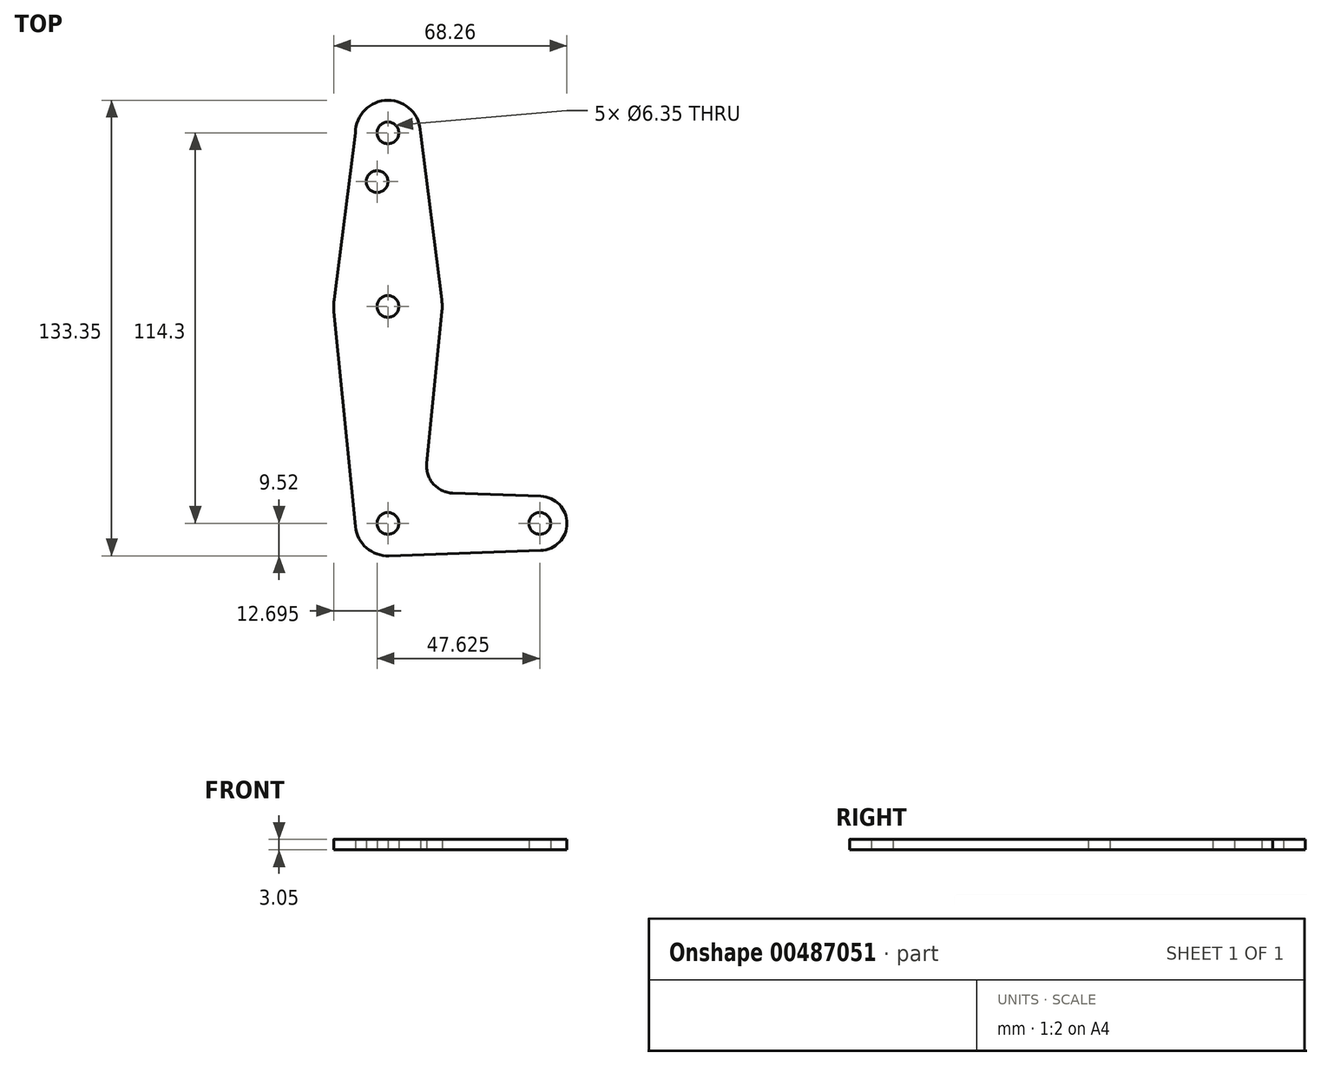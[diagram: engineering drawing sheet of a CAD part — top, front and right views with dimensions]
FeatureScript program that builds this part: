
annotation { "Feature Type Name" : "Feature", "Feature Type Description" : "" }
export const myFeature = defineFeature(function(context is Context, id is Id, definition is map)
    precondition{}
    {
        {
            var Q0;
            Q0=qCreatedBy(makeId("Top.planeOp"),FACE);
            var sketch = newSketch(context, id + "F0", { "sketchPlane" : qUnion([Q0])});
            skLineSegment(sketch, "E0", {"start": v(0, 0) * mm, "end": v(0, 114.3) * mm, "construction": true});
            skLineSegment(sketch, "E1", {"start": v(0, 0) * mm, "end": v(44.45, 0) * mm, "construction": true});
            skCircle(sketch, "E2", {"center": v(0, 0) * mm, "radius": 9.53 * mm});
            skCircle(sketch, "E3", {"center": v(0, 114.3) * mm, "radius": 9.53 * mm});
            skCircle(sketch, "E4", {"center": v(44.45, 0) * mm, "radius": 7.94 * mm});
            skCircle(sketch, "E5", {"center": v(0, 63.5) * mm, "radius": 15.88 * mm});
            skLineSegment(sketch, "E6", {"start": v(9.52, 114.3) * mm, "end": v(15.75, 65.5) * mm});
            skLineSegment(sketch, "E7", {"start": v(-9.52, 114.3) * mm, "end": v(-15.75, 65.5) * mm});
            skPoint(sketch, "E8.startSnap0", {"position": v(0, 57.15) * mm});
            skLineSegment(sketch, "E9", {"start": v(15.8, 61.91) * mm, "end": v(11.34, 17.6) * mm});
            skLineSegment(sketch, "E10", {"start": v(-15.8, 61.91) * mm, "end": v(-9.48, -0.95) * mm});
            skLineSegment(sketch, "E11", {"start": v(18.97, 8.85) * mm, "end": v(44.73, 7.93) * mm});
            skLineSegment(sketch, "E12", {"start": v(0.34, -9.52) * mm, "end": v(44.73, -7.93) * mm});
            skCircle(sketch, "E13", {"center": v(0, 114.3) * mm, "radius": 3.18 * mm});
            skCircle(sketch, "E14", {"center": v(0, 63.5) * mm, "radius": 3.18 * mm});
            skCircle(sketch, "E15", {"center": v(0, 0) * mm, "radius": 3.18 * mm});
            skCircle(sketch, "E16", {"center": v(44.45, 0) * mm, "radius": 3.18 * mm});
            skCircle(sketch, "E17", {"center": v(-3.18, 100.03) * mm, "radius": 3.18 * mm});
            skArc(sketch, "E18.filletArc", {"start": v(11.34, 17.6) * mm, "mid": v(13.26, 11.57) * mm, "end": v(18.97, 8.85) * mm});
            skSolve(sketch);
        }
        {
            var Q0;
            Q0=makeQuery(id+"F0.imprint","IMPRINT",FACE,{"disambiguationData":[TD([[makeQuery(id+"F0.imprint","IMPRINT",EDGE,{"derivedFrom":sQuery(id+"F0.wireOp",EDGE,"E13")}),-1.0]])]});
            var Q1;
            {var subQ0=sQuery(id+"F0.wireOp",EDGE,"E6");Q1=makeQuery(id+"F0.imprint","IMPRINT",FACE,{"disambiguationData":[TD([[makeQuery(id+"F0.imprint","IMPRINT",EDGE,{"derivedFrom":subQ0}),-1.0]])]});}
            var Q2;
            Q2=makeQuery(id+"F0.imprint","IMPRINT",FACE,{"disambiguationData":[TD([[makeQuery(id+"F0.imprint","IMPRINT",EDGE,{"derivedFrom":sQuery(id+"F0.wireOp",EDGE,"E14")}),-1.0]])]});
            var Q3;
            {var subQ0=sQuery(id+"F0.wireOp",EDGE,"E9");Q3=makeQuery(id+"F0.imprint","IMPRINT",FACE,{"disambiguationData":[TD([[makeQuery(id+"F0.imprint","IMPRINT",EDGE,{"derivedFrom":subQ0}),-1.0]])]});}
            var Q4;
            Q4=makeQuery(id+"F0.imprint","IMPRINT",FACE,{"disambiguationData":[TD([[makeQuery(id+"F0.imprint","IMPRINT",EDGE,{"derivedFrom":sQuery(id+"F0.wireOp",EDGE,"E15")}),-1.0]])]});
            var Q5;
            Q5=makeQuery(id+"F0.imprint","IMPRINT",FACE,{"disambiguationData":[TD([[makeQuery(id+"F0.imprint","IMPRINT",EDGE,{"derivedFrom":sQuery(id+"F0.wireOp",EDGE,"E16")}),-1.0]])]});
            extrude(context, id + "F1", {"entities" : qUnion([Q0, Q1, Q2, Q3, Q4, Q5]), "depth" : 3.05 * mm});
        }
    });
